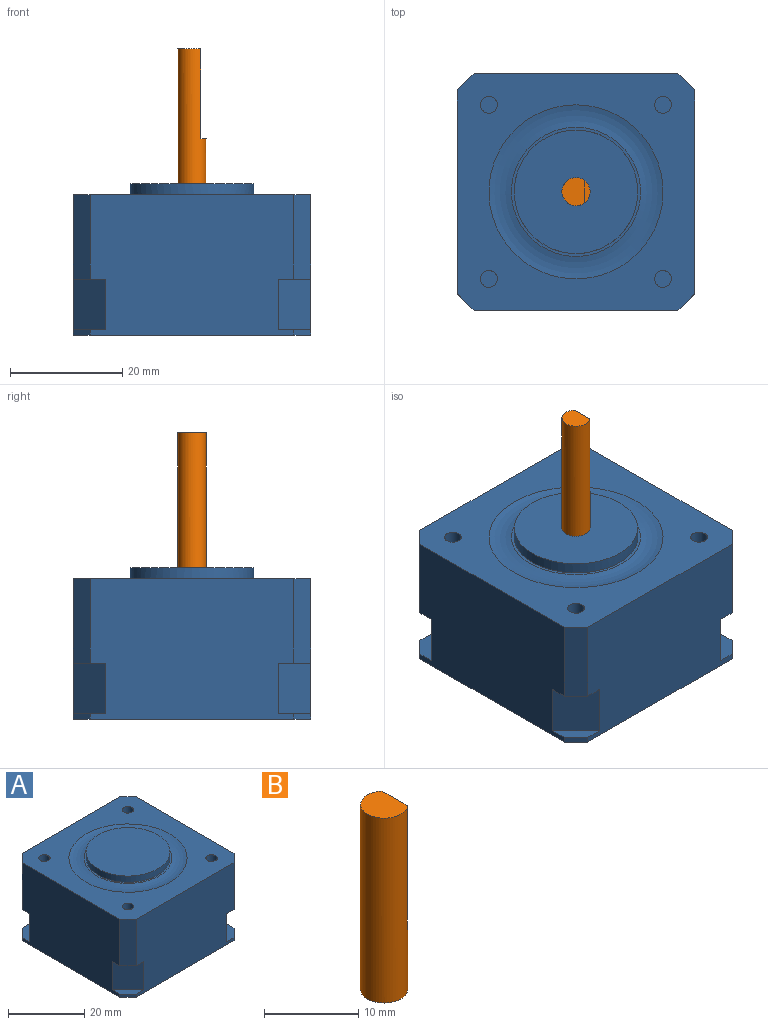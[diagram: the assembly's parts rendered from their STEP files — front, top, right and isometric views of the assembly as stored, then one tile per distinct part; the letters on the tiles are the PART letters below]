
ASSEMBLY  parts=2 mates=1
PART A: 58 faces, bbox 42.3x42.3x27.1 mm
  f0: plane 5.83x5.83mm, normal (0,0,1), area 12.5mm2, adj f3,f4,f5,f12
  f1: plane 5.83x5.83mm, normal (0,0,1), area 12.5mm2, adj f3,f9,f10,f13
  f2: plane 5.83x5.83mm, normal (0,0,1), area 12.5mm2, adj f7,f8,f9,f14
  f3: plane 36.3x25mm, normal (0,1,0), area 856.6mm2, adj f0,f1,f4,f10,f12,f13,f16,f18
  f4: plane 3x3mm, normal (-0.71,0.71,0), area 4.2mm2, adj f0,f3,f5,f37
  f5: plane 36.3x25mm, normal (-1,0,0), area 856.6mm2, adj f0,f4,f6,f11,f12,f15,f16,f19
  f6: plane 3x3mm, normal (-0.71,-0.71,0), area 4.2mm2, adj f5,f7,f11,f37
  f7: plane 36.3x25mm, normal (0,-1,0), area 856.6mm2, adj f2,f6,f8,f11,f14,f15,f16,f17
  f8: plane 3x3mm, normal (0.71,-0.71,0), area 4.2mm2, adj f2,f7,f9,f37
  f9: plane 36.3x25mm, normal (1,0,0), area 856.6mm2, adj f1,f2,f8,f10,f13,f14,f16,f17
  f10: plane 3x3mm, normal (0.71,0.71,0), area 4.2mm2, adj f1,f3,f9,f37
  f11: plane 5.83x5.83mm, normal (0,0,1), area 12.5mm2, adj f5,f6,f7,f15
  f12: plane 9x5.83mm, normal (-0.71,0.71,0), area 74.2mm2, adj f0,f3,f5,f19
  f13: plane 9x5.83mm, normal (0.71,0.71,0), area 74.2mm2, adj f1,f3,f9,f18
  f14: plane 9x5.83mm, normal (0.71,-0.71,0), area 74.2mm2, adj f2,f7,f9,f17
  f15: plane 9x5.83mm, normal (-0.71,-0.71,0), area 74.2mm2, adj f5,f7,f11,f24
  f16: plane 42.3x42.3mm, normal (0,0,1), area 988.2mm2, adj f3,f5,f7,f9,f20,f21,f22,f23
  f17: plane 5.83x5.83mm, normal (0,0,-1), area 12.5mm2, adj f7,f9,f14,f22
  f18: plane 5.83x5.83mm, normal (0,0,-1), area 12.5mm2, adj f3,f9,f13,f21
  f19: plane 5.83x5.83mm, normal (0,0,-1), area 12.5mm2, adj f3,f5,f12,f20
  f20: plane 15x3mm, normal (-0.71,0.71,0), area 63.6mm2, adj f3,f5,f16,f19
  f21: plane 15x3mm, normal (0.71,0.71,0), area 63.6mm2, adj f3,f9,f16,f18
  f22: plane 15x3mm, normal (0.71,-0.71,0), area 63.6mm2, adj f7,f9,f16,f17
  f23: plane 15x3mm, normal (-0.71,-0.71,0), area 63.6mm2, adj f5,f7,f16,f24
  f24: plane 5.83x5.83mm, normal (0,0,-1), area 12.5mm2, adj f5,f7,f15,f23
  f25: cylinder r=1.5mm len=5.5mm, axis (0,0,1), area 51.8mm2, adj f16,f26
  f26: plane 3x3mm, normal (0,0,1), area 7.1mm2, adj f25
  f27: cylinder r=1.5mm len=5.5mm, axis (0,0,1), area 51.8mm2, adj f16,f28
  f28: plane 3x3mm, normal (0,0,1), area 7.1mm2, adj f27
  f29: cylinder r=1.5mm len=5.5mm, axis (0,0,1), area 51.8mm2, adj f16,f30
  f30: plane 3x3mm, normal (0,0,1), area 7.1mm2, adj f29
  f31: cylinder r=1.5mm len=5.5mm, axis (0,0,1), area 51.8mm2, adj f16,f32
  f32: plane 3x3mm, normal (0,0,1), area 7.1mm2, adj f31
  f33: torus R=13.5mm, axis (0,0,-1), area 342.9mm2, adj f16,f34
  f34: plane 23x23mm, normal (0,0,1), area 35.3mm2, adj f33,f35
  f35: cylinder r=11mm len=22mm, axis (0,0,-1), area 138.2mm2, adj f34,f36
  f36: plane 22x22mm, normal (0,0,1), area 380.1mm2, adj f35
  f37: plane 42.3x42.3mm, normal (0,0,-1), area 1626mm2, adj f3,f4,f5,f6,f7,f8,f9,f10
  f38: plane 5x5mm, normal (0,0,-1), area 19.6mm2, adj f40
  f39: plane 8x8mm, normal (0,0,-1), area 30.6mm2, adj f40,f41
  f40: cylinder r=2.5mm len=5mm, axis (0,0,-1), area 15.7mm2, adj f38,f39
  f41: cylinder r=4mm len=8mm, axis (0,0,-1), area 50.3mm2, adj f37,f39
  f42: cylinder r=1.5mm len=4.5mm, axis (0,0,-1), area 42.4mm2, adj f43,f44
  f43: plane 3x3mm, normal (0,0,-1), area 7.1mm2, adj f42
  f44: plane 5.5x5.5mm, normal (0,0,-1), area 16.7mm2, adj f42,f45
  f45: cylinder r=2.75mm len=5.5mm, axis (0,0,-1), area 17.3mm2, adj f37,f44
  f46: cylinder r=1.5mm len=4.5mm, axis (0,0,-1), area 42.4mm2, adj f47,f48
  f47: plane 3x3mm, normal (0,0,-1), area 7.1mm2, adj f46
  f48: plane 5.5x5.5mm, normal (0,0,-1), area 16.7mm2, adj f46,f49
  f49: cylinder r=2.75mm len=5.5mm, axis (0,0,-1), area 17.3mm2, adj f37,f48
  f50: cylinder r=1.5mm len=4.5mm, axis (0,0,-1), area 42.4mm2, adj f51,f52
  f51: plane 3x3mm, normal (0,0,-1), area 7.1mm2, adj f50
  f52: plane 5.5x5.5mm, normal (0,0,-1), area 16.7mm2, adj f50,f53
  f53: cylinder r=2.75mm len=5.5mm, axis (0,0,-1), area 17.3mm2, adj f37,f52
  f54: cylinder r=1.5mm len=4.5mm, axis (0,0,-1), area 42.4mm2, adj f55,f56
  f55: plane 3x3mm, normal (0,0,-1), area 7.1mm2, adj f54
  f56: plane 5.5x5.5mm, normal (0,0,-1), area 16.7mm2, adj f54,f57
  f57: cylinder r=2.75mm len=5.5mm, axis (0,0,-1), area 17.3mm2, adj f37,f56
PART B: 5 faces, bbox 5x5x24 mm
  f0: cylinder r=2.5mm len=24mm, axis (0,0,-1), area 306.9mm2, adj f1,f2,f3,f4
  f1: plane 5x4.1mm, normal (0,0,1), area 17.2mm2, adj f0,f3
  f2: plane 5x5mm, normal (0,0,-1), area 19.6mm2, adj f0
  f3: plane 16x3.84mm, normal (1,0,0), area 61.5mm2, adj f0,f1,f4
  f4: plane 3.84x0.9mm, normal (0,0,1), area 2.4mm2, adj f0,f3
PLACE A t=(-23.72,55.46,1.23)mm
PLACE B t=(-23.72,5.46,1.23)mm
MATE revolute B.f0 <-> A.f35  axis (0,0,-1) through (-23.72,5.46,42.23)mm
